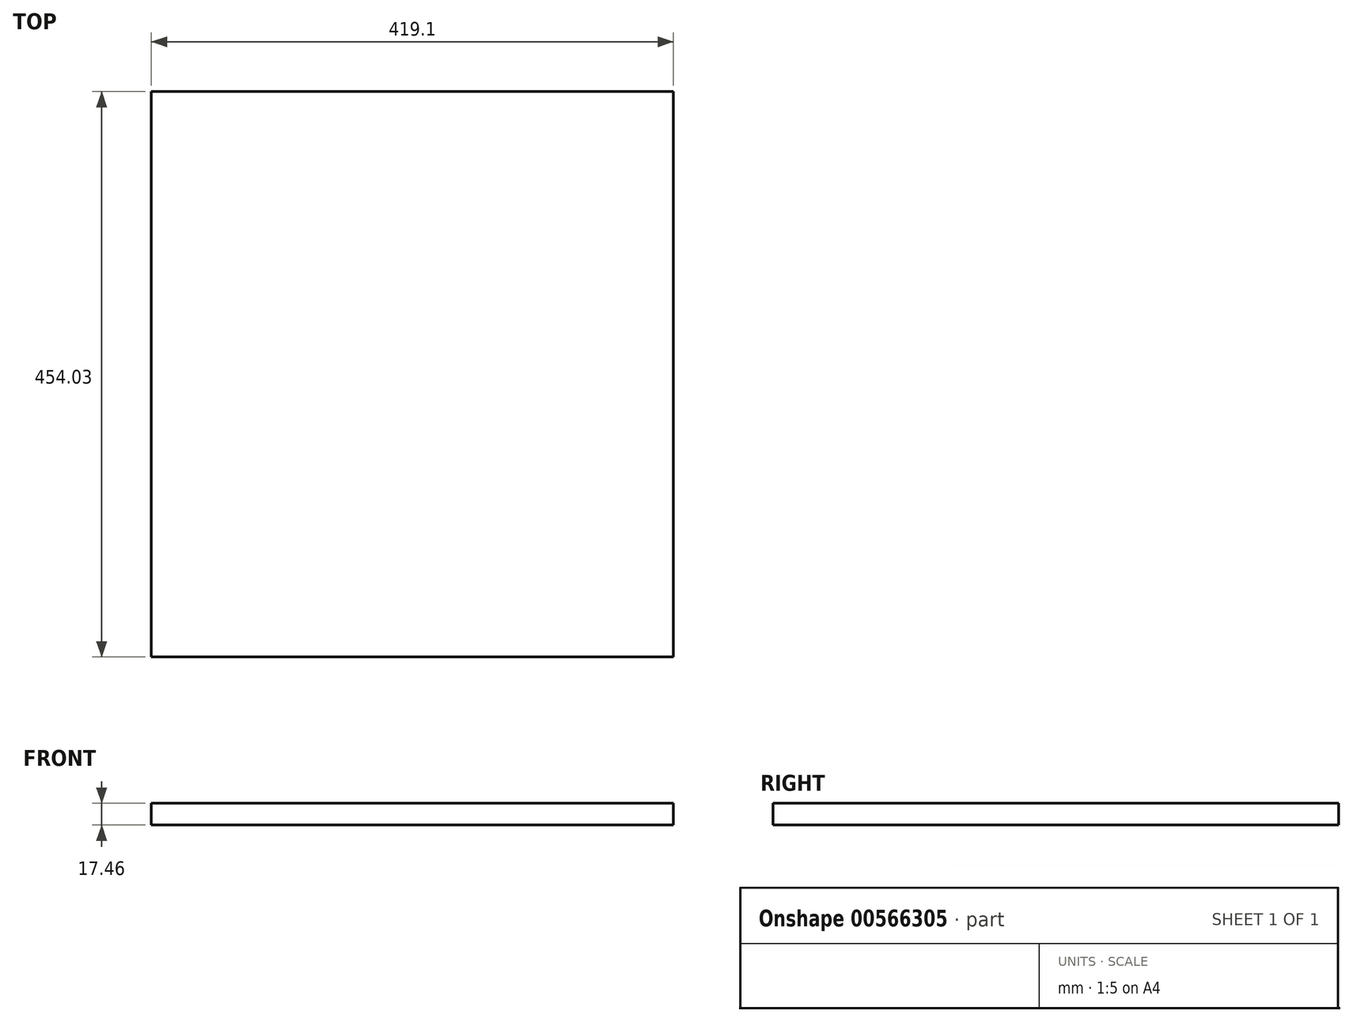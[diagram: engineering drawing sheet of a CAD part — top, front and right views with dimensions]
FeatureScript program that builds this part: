
annotation { "Feature Type Name" : "Feature", "Feature Type Description" : "" }
export const myFeature = defineFeature(function(context is Context, id is Id, definition is map)
    precondition{}
    {
        {
            var Q0;
            Q0=qCreatedBy(makeId("Top.planeOp"),FACE);
            var sketch = newSketch(context, id + "F0", { "sketchPlane" : qUnion([Q0])});
            skLineSegment(sketch, "E0.bottom", {"start": v(0, 0) * mm, "end": v(419.1, 0) * mm});
            skLineSegment(sketch, "E0.top", {"start": v(0, 454.03) * mm, "end": v(419.1, 454.03) * mm});
            skLineSegment(sketch, "E0.left", {"start": v(0, 0) * mm, "end": v(0, 454.03) * mm});
            skLineSegment(sketch, "E0.right", {"start": v(419.1, 0) * mm, "end": v(419.1, 454.03) * mm});
            skSolve(sketch);
        }
        {
            var Q0;
            Q0=makeQuery(id+"F0.imprint","IMPRINT",FACE,{"disambiguationData":[TD([[makeQuery(id+"F0.imprint","IMPRINT",EDGE,{"derivedFrom":sQuery(id+"F0.wireOp",EDGE,"E0.bottom")}),1.0]])]});
            extrude(context, id + "F1", {"entities" : qUnion([Q0]), "depth" : 17.46 * mm, "offsetDistance" : 25.4 * mm});
        }
    });
